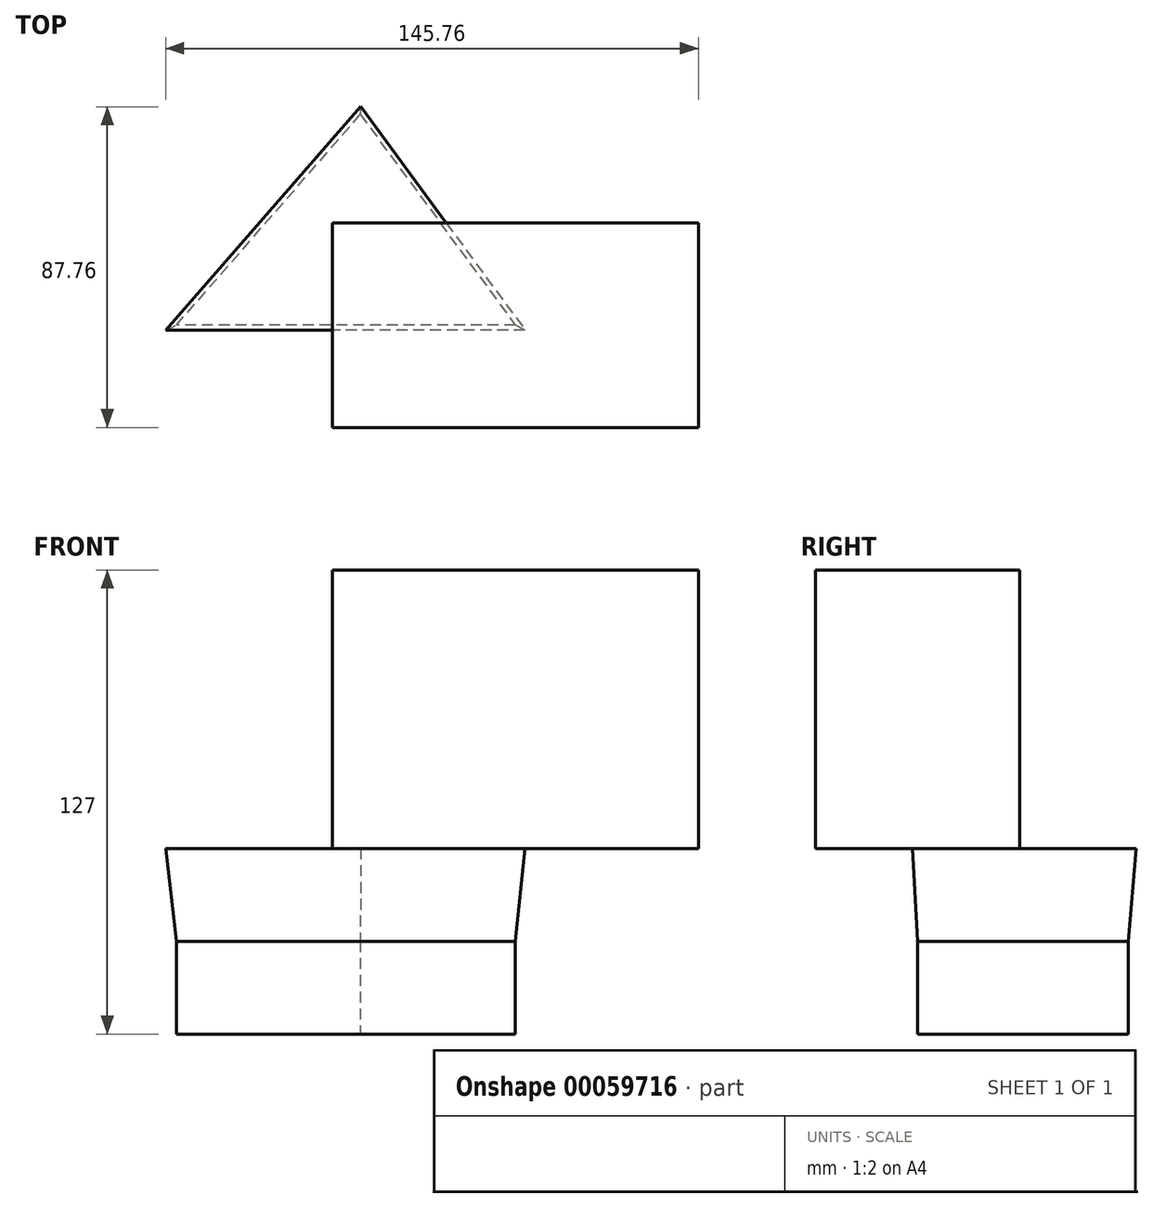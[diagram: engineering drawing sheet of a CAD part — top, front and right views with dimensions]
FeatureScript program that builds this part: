
annotation { "Feature Type Name" : "Feature", "Feature Type Description" : "" }
export const myFeature = defineFeature(function(context is Context, id is Id, definition is map)
    precondition{}
    {
        {
            var Q0;
            Q0=qCreatedBy(makeId("Top.planeOp"),FACE);
            var sketch = newSketch(context, id + "F0", { "sketchPlane" : qUnion([Q0])});
            skLineSegment(sketch, "E0", {"start": v(0, 0) * mm, "end": v(-92.76, 0) * mm});
            skLineSegment(sketch, "E1", {"start": v(-92.76, 0) * mm, "end": v(-42.42, 57.67) * mm});
            skLineSegment(sketch, "E2", {"start": v(-42.42, 57.67) * mm, "end": v(0, 0) * mm});
            skSolve(sketch);
        }
        {
            var Q0;
            Q0=makeQuery(id+"F0.imprint","IMPRINT",FACE,{"disambiguationData":[TD([[makeQuery(id+"F0.imprint","IMPRINT",EDGE,{"derivedFrom":sQuery(id+"F0.wireOp",EDGE,"E0")}),-1.0]])]});
            extrude(context, id + "F1", {"entities" : qUnion([Q0]), "depth" : 25.4 * mm, "hasDraft" : true, "draftAngle" : 3 * degree, "hasSecondDirection" : true, "secondDirectionOppositeDirection" : true, "secondDirectionDepth" : 25.4 * mm});
        }
        {
            var Q0;
            Q0=makeQuery(id+"F1.opExtrude","CAP_FACE",FACE,{"disambiguationData":[OSD([sQuery(id+"F0.wireOp",EDGE,"E0"),sQuery(id+"F0.wireOp",EDGE,"E1"),sQuery(id+"F0.wireOp",EDGE,"E2")])],"isStart":false});
            var sketch = newSketch(context, id + "F2", { "sketchPlane" : qUnion([Q0])});
            skLineSegment(sketch, "E3.rect.bottom", {"start": v(-50.07, 27.97) * mm, "end": v(50.07, 27.97) * mm});
            skLineSegment(sketch, "E3.rect.top", {"start": v(-50.07, -27.97) * mm, "end": v(50.07, -27.97) * mm});
            skLineSegment(sketch, "E3.rect.left", {"start": v(-50.07, 27.97) * mm, "end": v(-50.07, -27.97) * mm});
            skLineSegment(sketch, "E3.rect.right", {"start": v(50.07, 27.97) * mm, "end": v(50.07, -27.97) * mm});
            skPoint(sketch, "E3.rect.middle", {"position": v(0, 0) * mm});
            skSolve(sketch);
        }
        {
            var Q0;
            Q0 = qSketchRegion(id + "F2", true);
            extrude(context, id + "F3", {"entities" : qUnion([Q0]), "operationType" : NewBodyOperationType.ADD, "depth" : 76.2 * mm});
        }
        {
            var Q0;
            Q0=makeQuery(id+"F3.opExtrude","SWEPT_FACE",FACE,{"disambiguationData":[OSD([sQuery(id+"F2.wireOp",EDGE,"E3.rect.top")])]});
            var sketch = newSketch(context, id + "F6", { "sketchPlane" : qUnion([Q0])});
            skCircle(sketch, "E4", {"center": v(0, -147.57) * mm, "radius": 279.4 * mm});
            skSolve(sketch);
        }
    });
